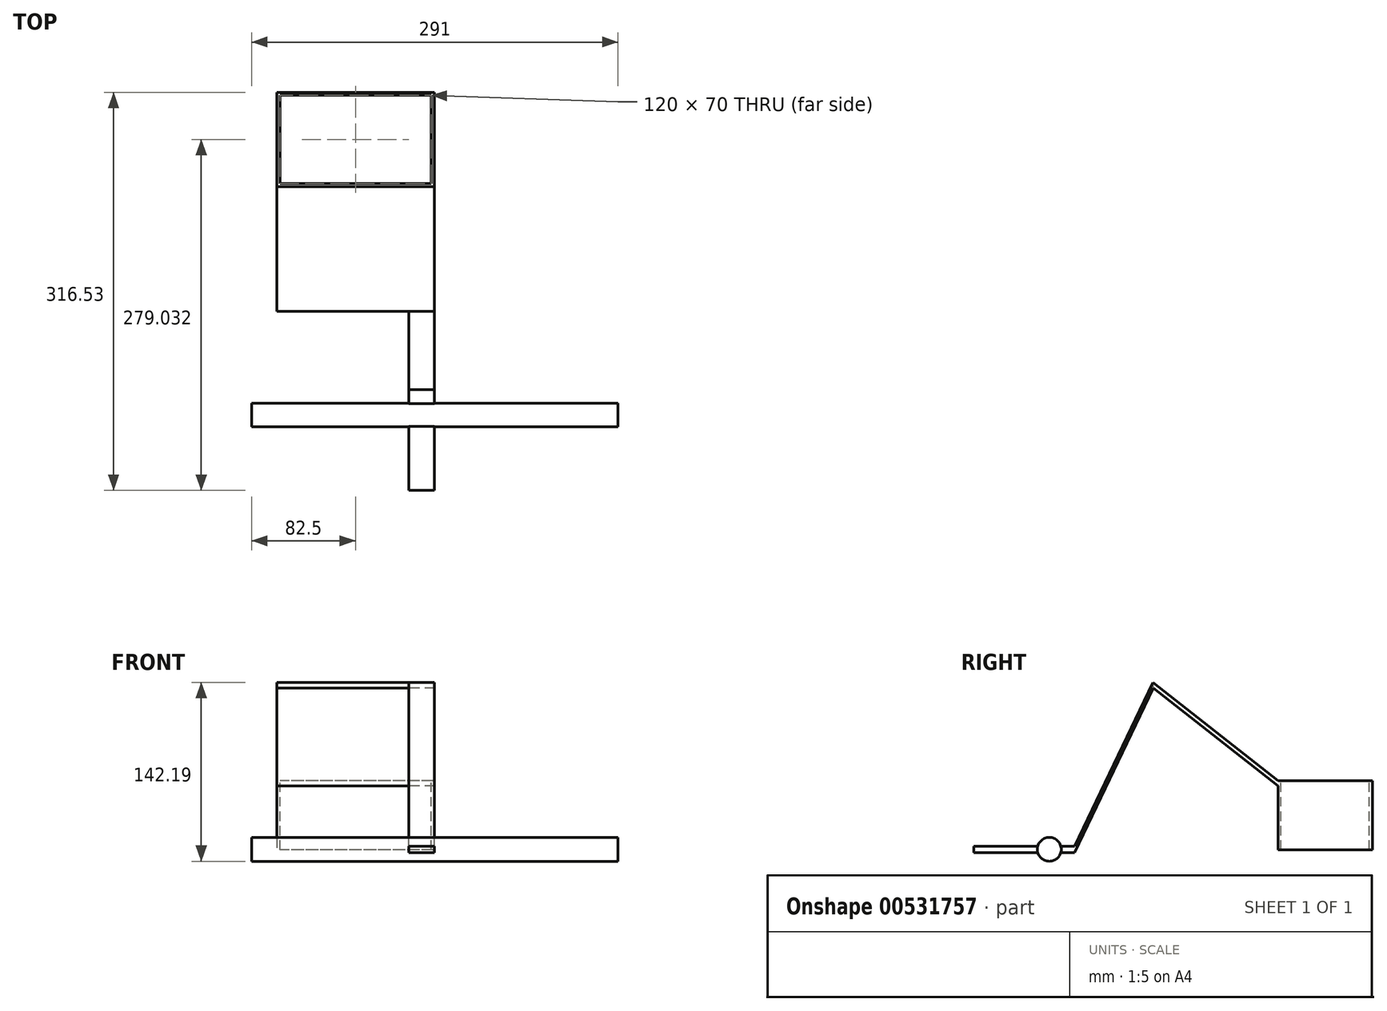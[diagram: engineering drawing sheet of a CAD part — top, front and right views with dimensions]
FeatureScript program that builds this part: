
annotation { "Feature Type Name" : "Feature", "Feature Type Description" : "" }
export const myFeature = defineFeature(function(context is Context, id is Id, definition is map)
    precondition{}
    {
        {
            var Q0;
            Q0=qCreatedBy(makeId("Right.planeOp"),FACE);
            var sketch = newSketch(context, id + "F0", { "sketchPlane" : qUnion([Q0])});
            skCircle(sketch, "E0", {"center": v(0, 0) * mm, "radius": 9.5 * mm});
            skSolve(sketch);
        }
        {
            var Q0;
            Q0 = qSketchRegion(id + "F0", true);
            extrude(context, id + "F1", {"entities" : qUnion([Q0]), "depth" : 291 * mm, "offsetDistance" : 25 * mm});
        }
        {
            var Q0;
            Q0=qCreatedBy(makeId("Front.planeOp"),FACE);
            var sketch = newSketch(context, id + "F2", { "sketchPlane" : qUnion([Q0])});
            skLineSegment(sketch, "E1", {"start": v(0, 0) * mm, "end": v(135, 0) * mm});
            skLineSegment(sketch, "E2.bottom", {"start": v(145, -2.5) * mm, "end": v(125, -2.5) * mm});
            skLineSegment(sketch, "E2.top", {"start": v(145, 2.5) * mm, "end": v(125, 2.5) * mm});
            skLineSegment(sketch, "E2.left", {"start": v(145, -2.5) * mm, "end": v(145, 2.5) * mm});
            skLineSegment(sketch, "E2.right", {"start": v(125, -2.5) * mm, "end": v(125, 2.5) * mm});
            skPoint(sketch, "E2.middle", {"position": v(135, 0) * mm});
            skSolve(sketch);
        }
        {
            var Q0;
            Q0 = qSketchRegion(id + "F2", true);
            extrude(context, id + "F3", {"entities" : qUnion([Q0]), "operationType" : NewBodyOperationType.ADD, "depth" : 60 * mm, "offsetDistance" : 25 * mm});
        }
        {
            var Q0;
            Q0 = qSketchRegion(id + "F2", true);
            extrude(context, id + "F4", {"entities" : qUnion([Q0]), "operationType" : NewBodyOperationType.ADD, "oppositeDirection" : true, "depth" : 20 * mm, "offsetDistance" : 25 * mm});
        }
        {
            var Q0;
            Q0=qCreatedBy(makeId("Right.planeOp"),FACE);
            cPlane(context, id + "F5", {"entities" : qUnion([Q0]), "cplaneType" : CPlaneType.OFFSET, "offset" : 125 * mm, "width" : 150 * mm, "height" : 150 * mm});
        }
        {
            var Q0;
            Q0=qCreatedBy(id+"F5.planeOp",FACE);
            var sketch = newSketch(context, id + "F6", { "sketchPlane" : qUnion([Q0])});
            skLineSegment(sketch, "E3", {"start": v(0, 0) * mm, "end": v(20, 0) * mm});
            skLineSegment(sketch, "E4", {"start": v(20, 0) * mm, "end": v(20, 2.5) * mm});
            skLineSegment(sketch, "E5", {"start": v(20, 2.5) * mm, "end": v(20, -2.5) * mm});
            skLineSegment(sketch, "E6", {"start": v(20, 2.5) * mm, "end": v(20, 54.44) * mm});
            skPoint(sketch, "E7.endSnap0", {"position": v(20, 28.47) * mm});
            skLineSegment(sketch, "E8", {"start": v(20, 2.5) * mm, "end": v(82.34, 132.7) * mm});
            skLineSegment(sketch, "E9", {"start": v(20, -2.5) * mm, "end": v(82.62, 128.28) * mm});
            skPoint(sketch, "E10.orphan", {"position": v(20, 132.7) * mm});
            skLineSegment(sketch, "E11", {"start": v(181.53, 54.58) * mm, "end": v(82.34, 132.7) * mm});
            skLineSegment(sketch, "E12", {"start": v(82.62, 128.28) * mm, "end": v(181.53, 50.39) * mm});
            skLineSegment(sketch, "E13", {"start": v(181.53, 50.39) * mm, "end": v(181.53, 54.58) * mm});
            skLineSegment(sketch, "E14", {"start": v(181.53, 54.58) * mm, "end": v(256.53, 54.58) * mm});
            skLineSegment(sketch, "E15", {"start": v(256.53, 54.58) * mm, "end": v(256.53, -0.42) * mm});
            skLineSegment(sketch, "E16", {"start": v(181.53, 50.39) * mm, "end": v(181.53, -0.42) * mm});
            skLineSegment(sketch, "E17", {"start": v(181.53, -0.42) * mm, "end": v(256.53, -0.42) * mm});
            skLineSegment(sketch, "E18", {"start": v(82.62, 128.28) * mm, "end": v(82.34, 132.7) * mm});
            skSolve(sketch);
        }
        {
            var Q0;
            {var subQ1=sQuery(id+"F6.wireOp",EDGE,"E8");Q0=makeQuery(id+"F6.imprint","IMPRINT",FACE,{"disambiguationData":[TD([[makeQuery(id+"F6.imprint","IMPRINT",EDGE,{"derivedFrom":subQ1}),-1.0]])]});}
            extrude(context, id + "F7", {"entities" : qUnion([Q0]), "operationType" : NewBodyOperationType.ADD, "depth" : 20 * mm, "offsetDistance" : 25 * mm});
        }
        {
            var Q0;
            Q0 = qSketchRegion(id + "F6", true);
            extrude(context, id + "F8", {"entities" : qUnion([Q0]), "operationType" : NewBodyOperationType.ADD, "depth" : 20 * mm, "offsetDistance" : 25 * mm});
        }
        {
            var Q0;
            {var subQ0=sQuery(id+"F6.wireOp",EDGE,"E9");var subQ1=sQuery(id+"F6.wireOp",EDGE,"E8");var subQ2=sQuery(id+"F6.wireOp",EDGE,"E5");Q0=makeQuery(id+"F8.boolean.opBoolean","MERGE",FACE,{"derivedFrom":[makeQuery(id+"F7.boolean.opBoolean","MERGE",FACE,{"derivedFrom":[makeQuery(id+"F4.opExtrude","SWEPT_FACE",FACE,{"disambiguationData":[OSD([sQuery(id+"F2.wireOp",EDGE,"E2.right")])]}),makeQuery(id+"F7.opExtrude","CAP_FACE",FACE,{"disambiguationData":[OSD([subQ2,subQ1,subQ0,sQuery(id+"F6.wireOp",EDGE,"E18")])],"isStart":true})]}),makeQuery(id+"F8.opExtrude","CAP_FACE",FACE,{"disambiguationData":[OSD([subQ2,subQ1,subQ0,sQuery(id+"F6.wireOp",EDGE,"E11"),sQuery(id+"F6.wireOp",EDGE,"E12"),sQuery(id+"F6.wireOp",EDGE,"E14"),sQuery(id+"F6.wireOp",EDGE,"E15"),sQuery(id+"F6.wireOp",EDGE,"E16"),sQuery(id+"F6.wireOp",EDGE,"E17")])],"isStart":true})]});}
            var sketch = newSketch(context, id + "F9", { "sketchPlane" : qUnion([Q0])});
            skLineSegment(sketch, "E19", {"start": v(-256.53, 54.58) * mm, "end": v(-181.53, 54.58) * mm});
            skLineSegment(sketch, "E20", {"start": v(-181.53, 54.58) * mm, "end": v(-181.53, -0.42) * mm});
            skLineSegment(sketch, "E21", {"start": v(-181.53, -0.42) * mm, "end": v(-256.53, -0.42) * mm});
            skLineSegment(sketch, "E22", {"start": v(-256.53, -0.42) * mm, "end": v(-256.53, 54.58) * mm});
            skLineSegment(sketch, "E23", {"start": v(-181.53, 50.39) * mm, "end": v(-82.62, 128.28) * mm});
            skLineSegment(sketch, "E24", {"start": v(-82.62, 128.28) * mm, "end": v(-82.34, 132.7) * mm});
            skLineSegment(sketch, "E25", {"start": v(-82.34, 132.7) * mm, "end": v(-181.53, 54.58) * mm});
            skSolve(sketch);
        }
        {
            var Q0;
            Q0 = qSketchRegion(id + "F9", true);
            extrude(context, id + "F10", {"entities" : qUnion([Q0]), "operationType" : NewBodyOperationType.ADD, "depth" : 105 * mm, "offsetDistance" : 25 * mm});
        }
        {
            var Q0;
            Q0=makeQuery(id+"F10.boolean.opBoolean","MERGE",FACE,{"derivedFrom":[makeQuery(id+"F8.opExtrude","SWEPT_FACE",FACE,{"disambiguationData":[OSD([sQuery(id+"F6.wireOp",EDGE,"E14")])]}),makeQuery(id+"F10.opExtrude","SWEPT_FACE",FACE,{"disambiguationData":[OSD([sQuery(id+"F9.wireOp",EDGE,"E19")])]})]});
            var sketch = newSketch(context, id + "F11", { "sketchPlane" : qUnion([Q0])});
            skLineSegment(sketch, "E26.bottom", {"start": v(142.5, 184.03) * mm, "end": v(22.5, 184.03) * mm});
            skLineSegment(sketch, "E26.top", {"start": v(142.5, 254.03) * mm, "end": v(22.5, 254.03) * mm});
            skLineSegment(sketch, "E26.left", {"start": v(142.5, 184.03) * mm, "end": v(142.5, 254.03) * mm});
            skLineSegment(sketch, "E26.right", {"start": v(22.5, 184.03) * mm, "end": v(22.5, 254.03) * mm});
            skPoint(sketch, "E26.middle", {"position": v(82.5, 219.03) * mm});
            skPoint(sketch, "E26.middle.positionSnap0", {"position": v(145, 219.03) * mm});
            skPoint(sketch, "E26.middle.positionSnap1", {"position": v(82.5, 181.53) * mm});
            skPoint(sketch, "E26.centerSnap0", {"position": v(145, 219.03) * mm});
            skPoint(sketch, "E26.centerSnap1", {"position": v(82.5, 181.53) * mm});
            skSolve(sketch);
        }
        {
            var Q0;
            Q0 = qSketchRegion(id + "F11", true);
            extrude(context, id + "F12", {"entities" : qUnion([Q0]), "operationType" : NewBodyOperationType.REMOVE, "oppositeDirection" : true, "depth" : 149.5 * mm, "offsetDistance" : 25 * mm});
        }
    });
